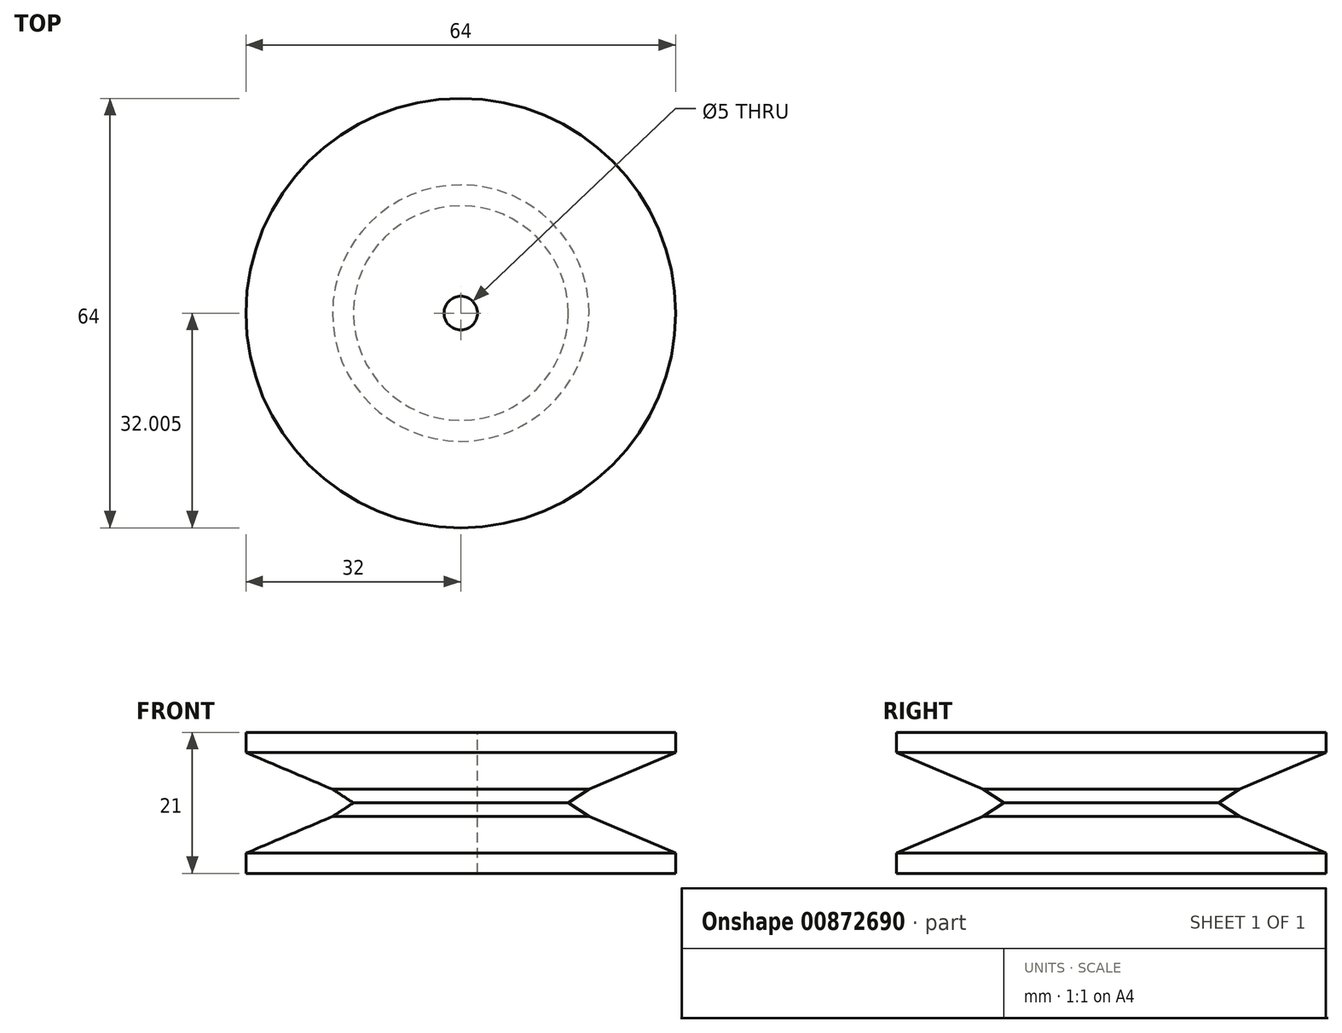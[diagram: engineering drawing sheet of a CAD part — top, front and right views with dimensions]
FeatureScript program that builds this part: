
annotation { "Feature Type Name" : "Feature", "Feature Type Description" : "" }
export const myFeature = defineFeature(function(context is Context, id is Id, definition is map)
    precondition{}
    {
        {
            var Q0;
            Q0=qCreatedBy(makeId("Right.planeOp"),FACE);
            var sketch = newSketch(context, id + "F0", { "sketchPlane" : qUnion([Q0])});
            skLineSegment(sketch, "E0.bottom", {"start": v(-128.8, 0) * mm, "end": v(-160.8, 0) * mm});
            skLineSegment(sketch, "E0.top", {"start": v(-128.8, 21) * mm, "end": v(-160.8, 21) * mm});
            skLineSegment(sketch, "E0.left", {"start": v(-128.8, 0) * mm, "end": v(-128.8, 21) * mm});
            skPoint(sketch, "E0.middle", {"position": v(-144.8, 10.5) * mm});
            skLineSegment(sketch, "E1", {"start": v(-160.8, 18) * mm, "end": v(-147.9, 12.53) * mm});
            skLineSegment(sketch, "E2", {"start": v(-147.9, 8.47) * mm, "end": v(-160.8, 3) * mm});
            skLineSegment(sketch, "E3", {"start": v(-160.8, 3) * mm, "end": v(-160.8, 0) * mm});
            skLineSegment(sketch, "E4", {"start": v(-160.8, 21) * mm, "end": v(-160.8, 18) * mm});
            skLineSegment(sketch, "E5", {"start": v(-147.9, 12.53) * mm, "end": v(-144.8, 10.5) * mm});
            skLineSegment(sketch, "E6", {"start": v(-144.8, 10.5) * mm, "end": v(-147.9, 8.47) * mm});
            skSolve(sketch);
        }
        {
            var Q0;
            Q0=makeQuery(id+"F0.imprint","IMPRINT",FACE,{"disambiguationData":[TD([[makeQuery(id+"F0.imprint","IMPRINT",EDGE,{"derivedFrom":sQuery(id+"F0.wireOp",EDGE,"E0.bottom")}),-1.0]])]});
            var Q1;
            Q1=sQuery(id+"F0.wireOp",EDGE,"E0.left");
            revolve(context, id + "F1", {"surfaceOperationType" : NewSurfaceOperationType.NEW, "entities" : qUnion([Q0]), "axis" : qUnion([Q1]), "revolveType" : RevolveType.FULL});
        }
        {
            var Q0;
            Q0=makeQuery(id+"F1.opRevolve","SWEPT_FACE",FACE,{"disambiguationData":[OSD([sQuery(id+"F0.wireOp",EDGE,"E0.top")])]});
            var sketch = newSketch(context, id + "F2", { "sketchPlane" : qUnion([Q0])});
            skCircle(sketch, "E7", {"center": v(0, -128.8) * mm, "radius": 2.5 * mm});
            skSolve(sketch);
        }
        {
            var Q0;
            Q0=makeQuery(id+"F2.imprint","IMPRINT",FACE,{"disambiguationData":[TD([[makeQuery(id+"F2.imprint","IMPRINT",EDGE,{"derivedFrom":sQuery(id+"F2.wireOp",EDGE,"E7")}),1.0]])]});
            var Q1;
            Q1=sQuery(id+"F2.wireOp",EDGE,"E7");
            var Q2;
            Q2=makeQuery(id+"F1.opRevolve","SWEPT_FACE",FACE,{"disambiguationData":[OSD([sQuery(id+"F0.wireOp",EDGE,"E0.bottom")])]});
            extrude(context, id + "F3", {"entities" : qUnion([Q0]), "operationType" : NewBodyOperationType.REMOVE, "surfaceEntities" : qUnion([Q1]), "endBound" : BoundingType.UP_TO_SURFACE, "oppositeDirection" : true, "depth" : 5 * mm, "endBoundEntityFace" : qUnion([Q2]), "offsetDistance" : 25 * mm});
        }
    });
